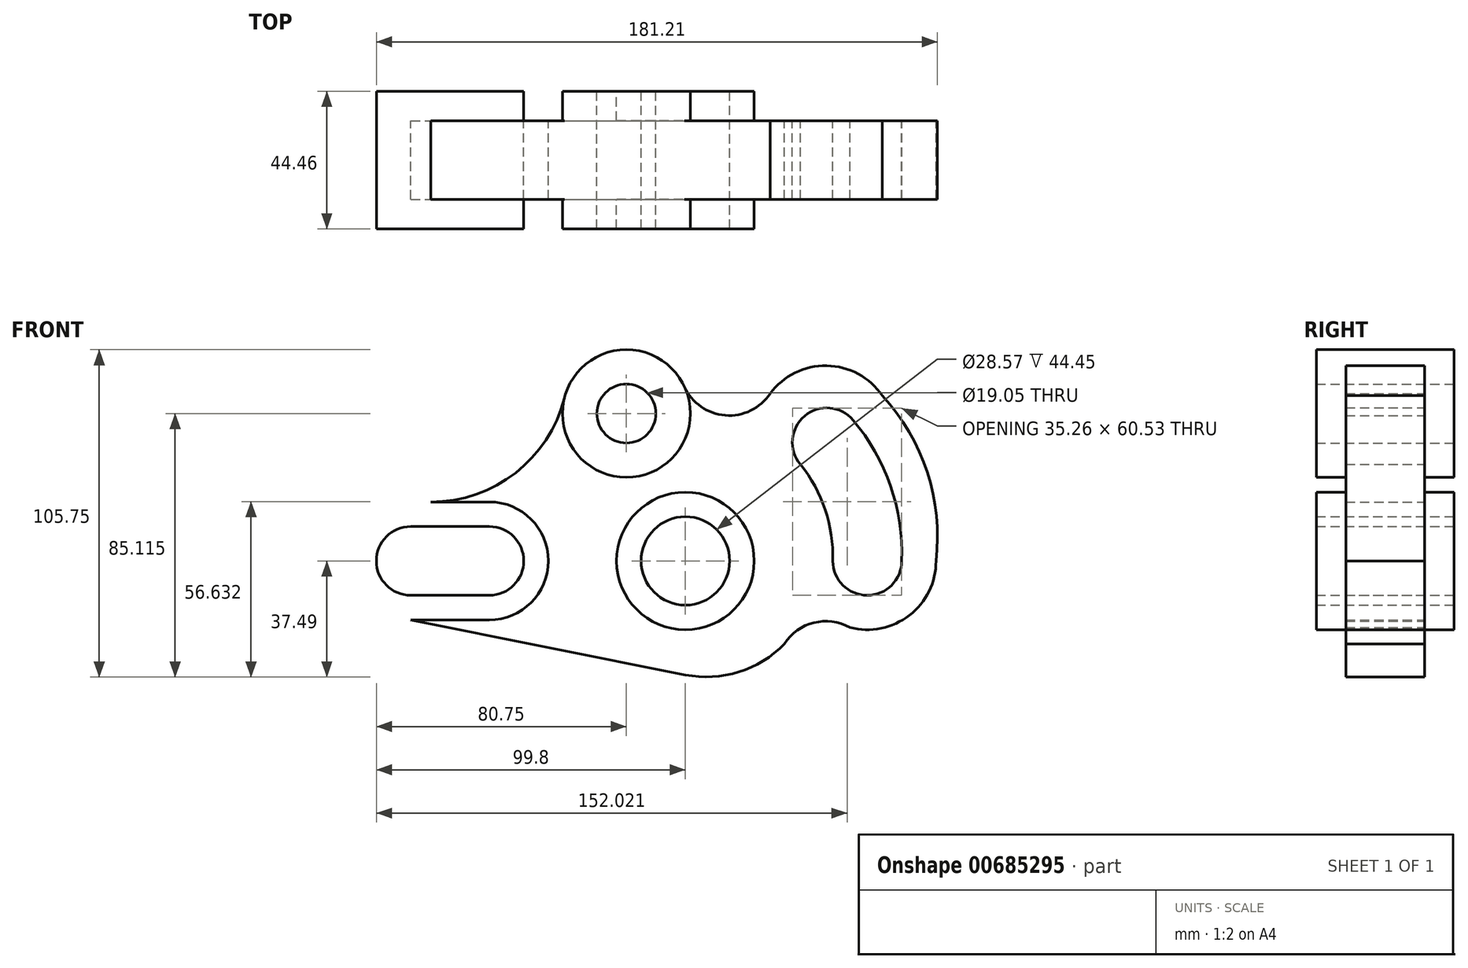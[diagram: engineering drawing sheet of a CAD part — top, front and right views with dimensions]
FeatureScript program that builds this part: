
annotation { "Feature Type Name" : "Feature", "Feature Type Description" : "" }
export const myFeature = defineFeature(function(context is Context, id is Id, definition is map)
    precondition{}
    {
        {
            var Q0;
            Q0=qCreatedBy(makeId("Front.planeOp"),FACE);
            var sketch = newSketch(context, id + "F0", { "sketchPlane" : qUnion([Q0])});
            skCircle(sketch, "E0", {"center": v(0, 0) * mm, "radius": 14.29 * mm});
            skCircle(sketch, "E1", {"center": v(0, 0) * mm, "radius": 22.23 * mm});
            skLineSegment(sketch, "E2", {"start": v(0, 0) * mm, "end": v(0, 96.95) * mm, "construction": true});
            skLineSegment(sketch, "E3", {"start": v(-19.05, 96.3) * mm, "end": v(-19.05, 0) * mm, "construction": true});
            skLineSegment(sketch, "E4", {"start": v(0, 0) * mm, "end": v(-159.9, 0) * mm, "construction": true});
            skLineSegment(sketch, "E5", {"start": v(0, 47.63) * mm, "end": v(-161.17, 47.62) * mm, "construction": true});
            skPoint(sketch, "E6", {"position": v(-19.05, 47.63) * mm});
            skCircle(sketch, "E7", {"center": v(-19.05, 47.63) * mm, "radius": 20.64 * mm});
            skCircle(sketch, "E8", {"center": v(-19.05, 47.63) * mm, "radius": 9.53 * mm});
            skLineSegment(sketch, "E9", {"start": v(0, 0) * mm, "end": v(147.71, 123.95) * mm, "construction": true});
            skLineSegment(sketch, "E10", {"start": v(0, 0) * mm, "end": v(182.4, 0) * mm, "construction": true});
            skLineSegment(sketch, "E11", {"start": v(0, 0) * mm, "end": v(0, -110.42) * mm, "construction": true});
            skLineSegment(sketch, "E12", {"start": v(58.72, 0) * mm, "end": v(58.72, -110.8) * mm, "construction": true});
            skArc(sketch, "E13", {"start": v(69.85, 0) * mm, "mid": v(58.72, -11.13) * mm, "end": v(47.6, 0) * mm});
            skLineSegment(sketch, "E14", {"start": v(-88.7, 0) * mm, "end": v(-88.7, -107.55) * mm, "construction": true});
            skArc(sketch, "E15", {"start": v(-88.7, -11.1) * mm, "mid": v(-99.8, 0) * mm, "end": v(-88.7, 11.1) * mm});
            skArc(sketch, "E16", {"start": v(-88.7, 19.05) * mm, "mid": v(-107.75, 0) * mm, "end": v(-88.7, -19.05) * mm});
            skPoint(sketch, "E17", {"position": v(-63.3, 0) * mm});
            skLineSegment(sketch, "E18", {"start": v(-88.7, 11.1) * mm, "end": v(-63.3, 11.1) * mm});
            skLineSegment(sketch, "E19", {"start": v(-88.7, -11.1) * mm, "end": v(-63.3, -11.1) * mm});
            skLineSegment(sketch, "E20", {"start": v(-88.7, -19.05) * mm, "end": v(-63.3, -19.05) * mm});
            skLineSegment(sketch, "E21", {"start": v(-88.7, 19.05) * mm, "end": v(-63.3, 19.05) * mm});
            skArc(sketch, "E22", {"start": v(-63.3, 11.1) * mm, "mid": v(-52.2, 0) * mm, "end": v(-63.3, -11.1) * mm});
            skArc(sketch, "E23", {"start": v(-63.3, 19.05) * mm, "mid": v(-44.25, 0) * mm, "end": v(-63.3, -19.05) * mm});
            skArc(sketch, "E24", {"start": v(47.6, 0) * mm, "mid": v(45.16, 16.52) * mm, "end": v(37.15, 31.17) * mm});
            skArc(sketch, "E25", {"start": v(69.85, 0) * mm, "mid": v(66.24, 24.19) * mm, "end": v(54.2, 45.48) * mm});
            skArc(sketch, "E26", {"start": v(58.72, 0) * mm, "mid": v(55.37, 20.24) * mm, "end": v(45.67, 38.33) * mm, "construction": true});
            skArc(sketch, "E27", {"start": v(37.15, 31.17) * mm, "mid": v(38.52, 46.85) * mm, "end": v(54.2, 45.48) * mm});
            skArc(sketch, "E28", {"start": v(-82.17, 19.05) * mm, "mid": v(-54.84, 28.45) * mm, "end": v(-39.06, 52.66) * mm});
            skArc(sketch, "E29", {"start": v(53.14, -21.51) * mm, "mid": v(72.32, -17.58) * mm, "end": v(80.95, 0) * mm});
            skArc(sketch, "E30", {"start": v(53.14, -21.51) * mm, "mid": v(41.5, -19.96) * mm, "end": v(31.98, -26.82) * mm});
            skLineSegment(sketch, "E31", {"start": v(-88.7, -19.05) * mm, "end": v(0, -36.8) * mm});
            skArc(sketch, "E32", {"start": v(0, -36.8) * mm, "mid": v(17.27, -35.9) * mm, "end": v(31.98, -26.82) * mm});
            skArc(sketch, "E33", {"start": v(-0.3, 56.23) * mm, "mid": v(12.9, 47.02) * mm, "end": v(27.36, 54.06) * mm});
            skArc(sketch, "E34", {"start": v(63.6, 53.37) * mm, "mid": v(45.66, 63.08) * mm, "end": v(27.36, 54.06) * mm});
            skArc(sketch, "E35", {"start": v(80.95, 0) * mm, "mid": v(78.12, 28.59) * mm, "end": v(63.6, 53.37) * mm});
            skSolve(sketch);
        }
        {
            var Q0;
            Q0=makeQuery(id+"F0.imprint","IMPRINT",FACE,{"disambiguationData":[TD([[makeQuery(id+"F0.imprint","IMPRINT",EDGE,{"derivedFrom":sQuery(id+"F0.wireOp",EDGE,"E1")}),-1.0]])]});
            extrude(context, id + "F1", {"entities" : qUnion([Q0]), "depth" : 25.4 * mm, "offsetDistance" : 25.4 * mm, "symmetric" : true});
        }
        {
            var Q0;
            Q0=makeQuery(id+"F0.imprint","IMPRINT",FACE,{"disambiguationData":[TD([[makeQuery(id+"F0.imprint","IMPRINT",EDGE,{"derivedFrom":sQuery(id+"F0.wireOp",EDGE,"E8")}),-1.0]])]});
            var Q1;
            Q1=makeQuery(id+"F0.imprint","IMPRINT",FACE,{"disambiguationData":[TD([[makeQuery(id+"F0.imprint","IMPRINT",EDGE,{"derivedFrom":sQuery(id+"F0.wireOp",EDGE,"E0")}),-1.0]])]});
            var Q2;
            Q2=makeQuery(id+"F0.imprint","IMPRINT",FACE,{"disambiguationData":[TD([[makeQuery(id+"F0.imprint","IMPRINT",EDGE,{"derivedFrom":sQuery(id+"F0.wireOp",EDGE,"E15")}),1.0]])]});
            extrude(context, id + "F2", {"entities" : qUnion([Q0, Q1, Q2]), "operationType" : NewBodyOperationType.ADD, "depth" : 44.45 * mm, "offsetDistance" : 25.4 * mm, "symmetric" : true});
        }
    });
